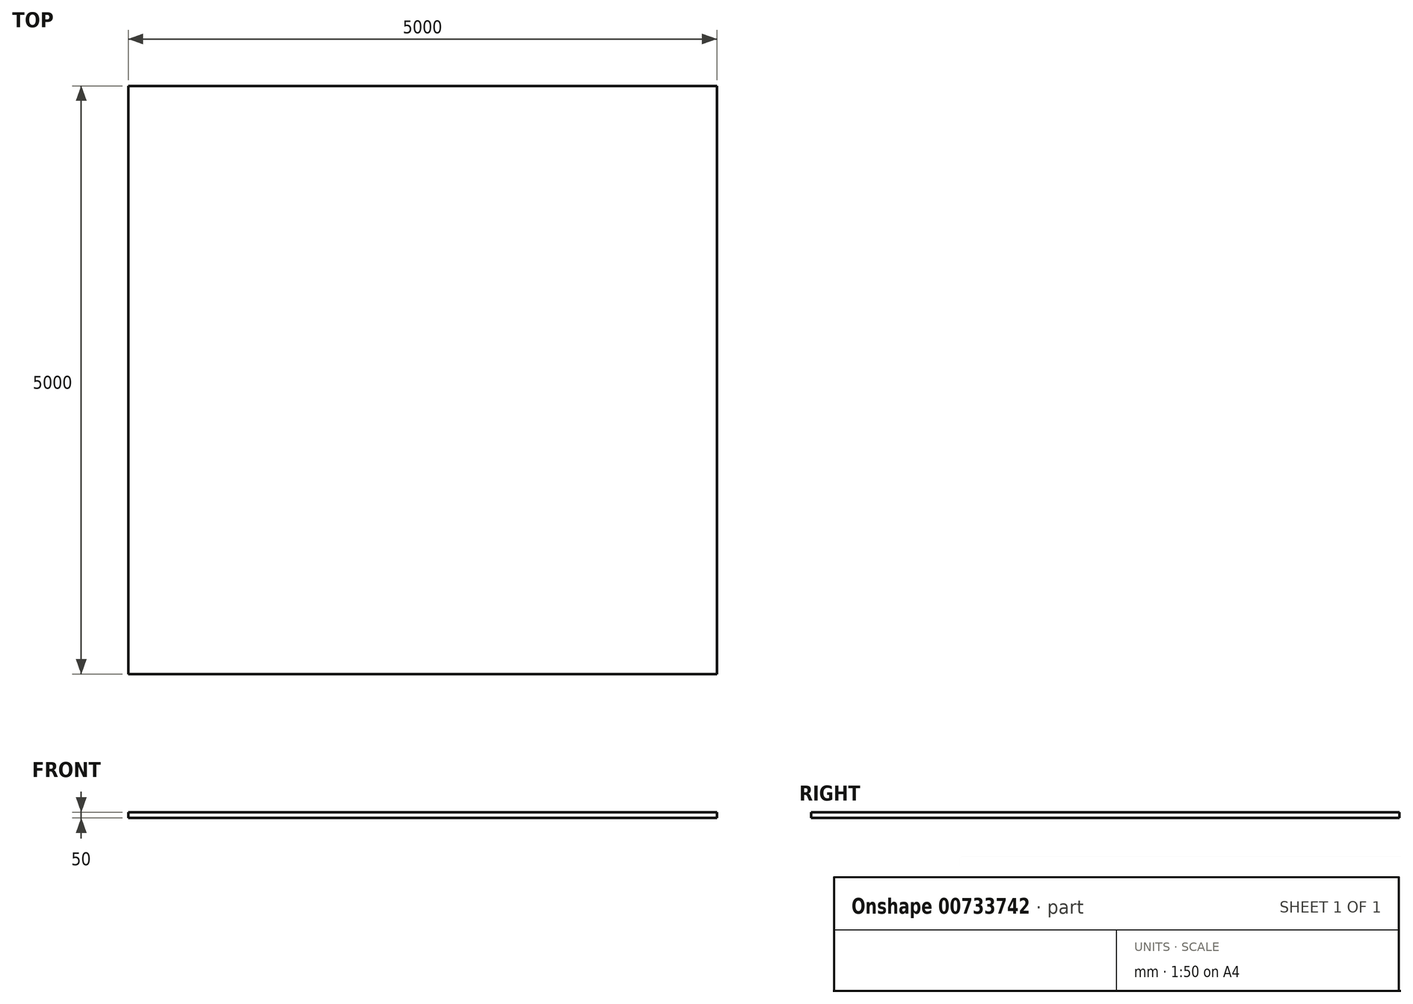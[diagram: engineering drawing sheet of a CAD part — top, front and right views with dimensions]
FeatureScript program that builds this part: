
annotation { "Feature Type Name" : "Feature", "Feature Type Description" : "" }
export const myFeature = defineFeature(function(context is Context, id is Id, definition is map)
    precondition{}
    {
        {
            var Q0;
            Q0=qCreatedBy(makeId("Top.planeOp"),FACE);
            var sketch = newSketch(context, id + "F0", { "sketchPlane" : qUnion([Q0])});
            skLineSegment(sketch, "E0.bottom", {"start": v(2495.42, -2500) * mm, "end": v(-2504.58, -2500) * mm});
            skLineSegment(sketch, "E0.top", {"start": v(2495.42, 2500) * mm, "end": v(-2504.58, 2500) * mm});
            skLineSegment(sketch, "E0.left", {"start": v(2495.42, -2500) * mm, "end": v(2495.42, 2500) * mm});
            skLineSegment(sketch, "E0.right", {"start": v(-2504.58, -2500) * mm, "end": v(-2504.58, 2500) * mm});
            skPoint(sketch, "E0.middle", {"position": v(-4.58, 0) * mm});
            skSolve(sketch);
        }
        {
            var Q0;
            Q0=makeQuery(id+"F0.imprint","IMPRINT",FACE,{"disambiguationData":[TD([[makeQuery(id+"F0.imprint","IMPRINT",EDGE,{"derivedFrom":sQuery(id+"F0.wireOp",EDGE,"E0.bottom")}),-1.0]])]});
            extrude(context, id + "F1", {"entities" : qUnion([Q0]), "depth" : 50 * mm, "offsetDistance" : 25 * mm});
        }
    });
